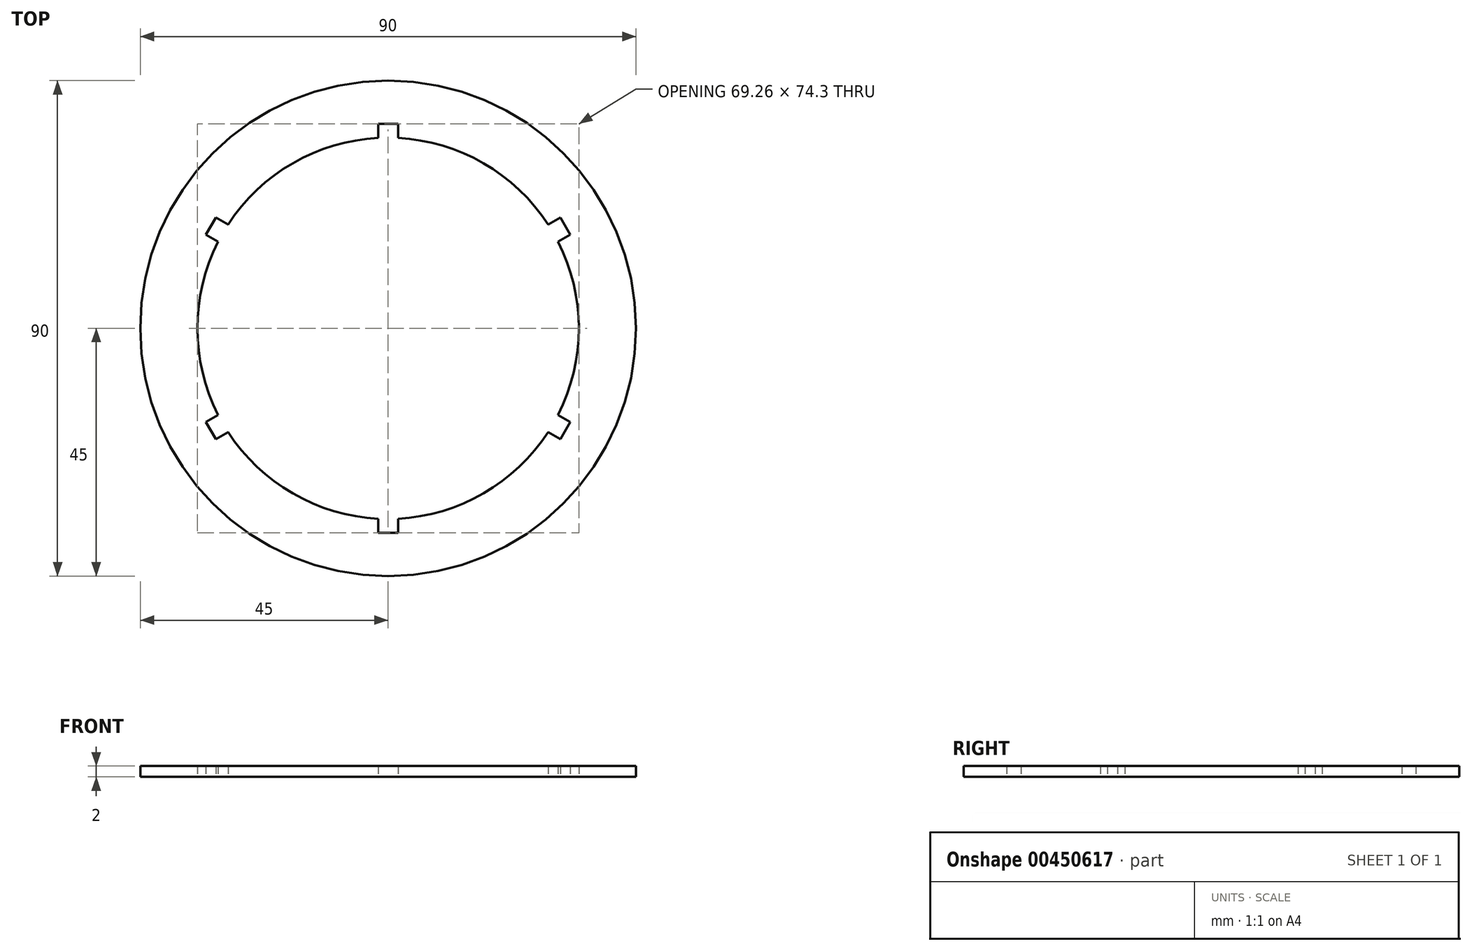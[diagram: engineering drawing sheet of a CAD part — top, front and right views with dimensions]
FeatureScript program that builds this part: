
annotation { "Feature Type Name" : "Feature", "Feature Type Description" : "" }
export const myFeature = defineFeature(function(context is Context, id is Id, definition is map)
    precondition{}
    {
        {
            var Q0;
            Q0=qCreatedBy(makeId("Top.planeOp"),FACE);
            var sketch = newSketch(context, id + "F0", { "sketchPlane" : qUnion([Q0])});
            skCircle(sketch, "E0", {"center": v(0, 0) * mm, "radius": 45 * mm});
            skCircle(sketch, "E1", {"center": v(0, 0) * mm, "radius": 34.63 * mm, "construction": true});
            skLineSegment(sketch, "E2", {"start": v(0, 34.63) * mm, "end": v(0, 37.15) * mm, "construction": true});
            skLineSegment(sketch, "E3", {"start": v(1.81, 37.15) * mm, "end": v(-1.81, 37.15) * mm});
            skLineSegment(sketch, "E4", {"start": v(-1.81, 37.15) * mm, "end": v(-1.8, 34.58) * mm});
            skLineSegment(sketch, "E5", {"start": v(1.8, 37.15) * mm, "end": v(1.81, 34.58) * mm});
            skArc(sketch, "E6", {"start": v(29.04, 18.86) * mm, "mid": v(17.31, 30) * mm, "end": v(1.81, 34.58) * mm});
            skLineSegment(sketch, "E7.1.0", {"start": v(-33.08, 17) * mm, "end": v(-30.85, 15.72) * mm});
            skLineSegment(sketch, "E7.1.1", {"start": v(-31.27, 20.14) * mm, "end": v(-33.08, 17) * mm});
            skLineSegment(sketch, "E7.1.2", {"start": v(-31.27, 20.14) * mm, "end": v(-29.04, 18.86) * mm});
            skArc(sketch, "E7.1.3", {"start": v(-1.8, 34.58) * mm, "mid": v(-17.31, 30) * mm, "end": v(-29.04, 18.86) * mm});
            skLineSegment(sketch, "E7.2.0", {"start": v(-31.27, -20.14) * mm, "end": v(-29.04, -18.86) * mm});
            skLineSegment(sketch, "E7.2.1", {"start": v(-33.08, -17) * mm, "end": v(-31.27, -20.14) * mm});
            skLineSegment(sketch, "E7.2.2", {"start": v(-33.08, -17) * mm, "end": v(-30.85, -15.72) * mm});
            skArc(sketch, "E7.2.3", {"start": v(-30.85, 15.72) * mm, "mid": v(-34.63, 0) * mm, "end": v(-30.85, -15.72) * mm});
            skLineSegment(sketch, "E8.2.3.0", {"start": v(1.8, -37.15) * mm, "end": v(1.8, -34.58) * mm});
            skLineSegment(sketch, "E8.3.3.0", {"start": v(-1.81, -37.15) * mm, "end": v(1.8, -37.15) * mm});
            skLineSegment(sketch, "E8.6.3.0", {"start": v(-1.81, -37.15) * mm, "end": v(-1.81, -34.58) * mm});
            skArc(sketch, "E8.9.3.0", {"start": v(-29.04, -18.86) * mm, "mid": v(-17.32, -30) * mm, "end": v(-1.81, -34.58) * mm});
            skLineSegment(sketch, "E8.2.4.0", {"start": v(33.08, -17) * mm, "end": v(30.85, -15.72) * mm});
            skLineSegment(sketch, "E8.3.4.0", {"start": v(31.27, -20.14) * mm, "end": v(33.08, -17) * mm});
            skLineSegment(sketch, "E8.6.4.0", {"start": v(31.27, -20.14) * mm, "end": v(29.04, -18.86) * mm});
            skArc(sketch, "E8.9.4.0", {"start": v(1.8, -34.58) * mm, "mid": v(17.31, -30) * mm, "end": v(29.04, -18.86) * mm});
            skLineSegment(sketch, "E8.2.5.0", {"start": v(31.27, 20.14) * mm, "end": v(29.04, 18.86) * mm});
            skLineSegment(sketch, "E8.3.5.0", {"start": v(33.08, 17) * mm, "end": v(31.27, 20.14) * mm});
            skLineSegment(sketch, "E8.6.5.0", {"start": v(33.08, 17) * mm, "end": v(30.85, 15.72) * mm});
            skArc(sketch, "E8.9.5.0", {"start": v(30.85, -15.72) * mm, "mid": v(34.63, 0) * mm, "end": v(30.85, 15.72) * mm});
            skSolve(sketch);
        }
        {
            var Q0;
            Q0 = qSketchRegion(id + "F0", true);
            extrude(context, id + "F1", {"entities" : qUnion([Q0]), "depth" : 2 * mm});
        }
    });
